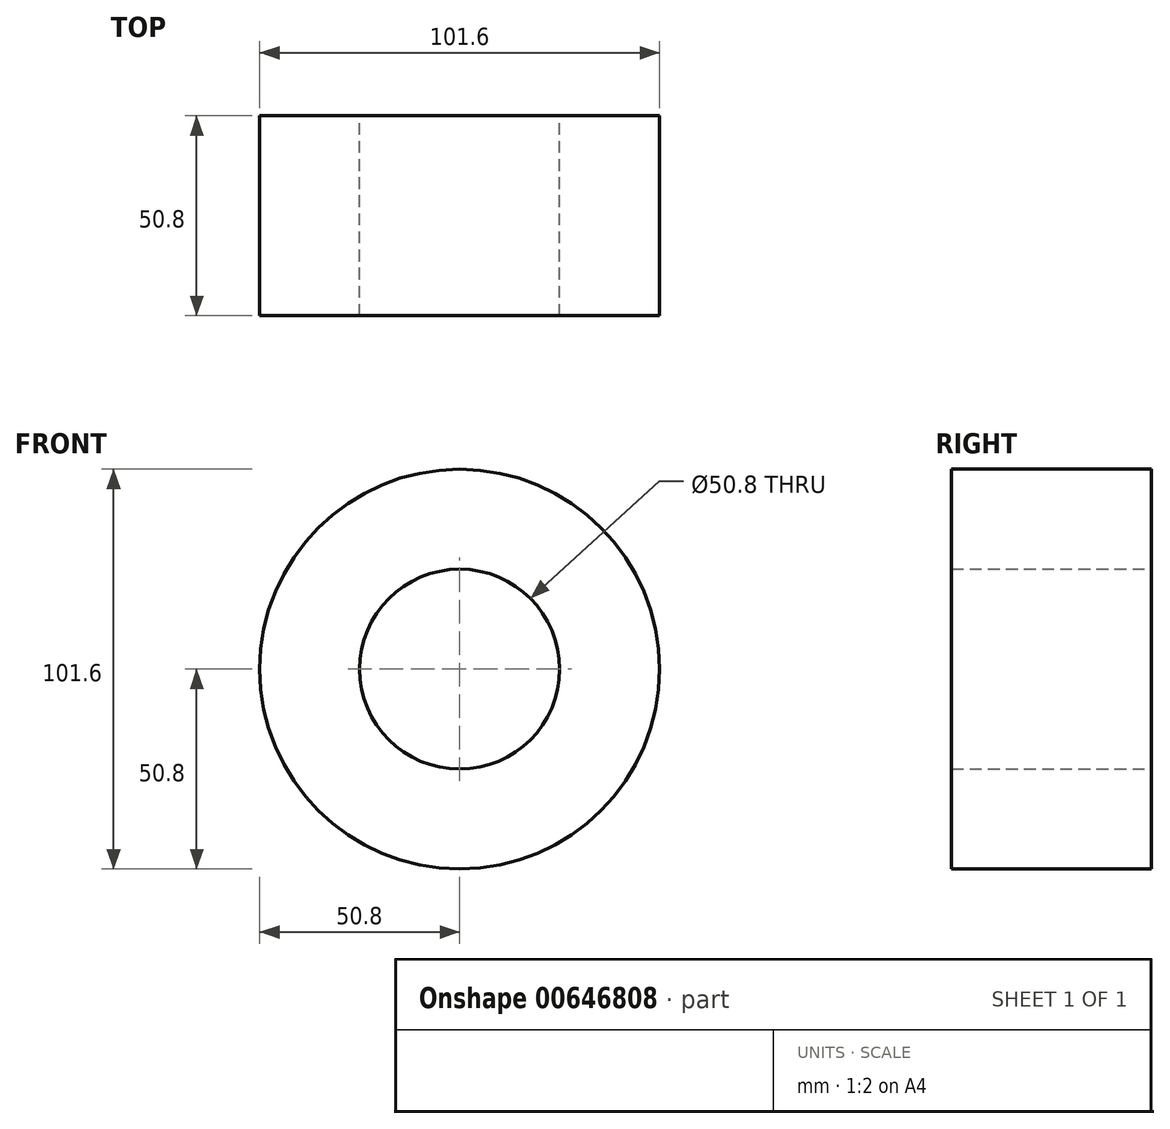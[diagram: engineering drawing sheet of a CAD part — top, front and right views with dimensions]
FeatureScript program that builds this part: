
annotation { "Feature Type Name" : "Feature", "Feature Type Description" : "" }
export const myFeature = defineFeature(function(context is Context, id is Id, definition is map)
    precondition{}
    {
        {
            var Q0;
            Q0=qCreatedBy(makeId("Front.planeOp"),FACE);
            var sketch = newSketch(context, id + "F0", { "sketchPlane" : qUnion([Q0])});
            skCircle(sketch, "E0", {"center": v(0, 0) * mm, "radius": 25.4 * mm});
            skCircle(sketch, "E1", {"center": v(0, 0) * mm, "radius": 50.8 * mm});
            skSolve(sketch);
        }
        {
            var Q0;
            Q0=makeQuery(id+"F0.imprint","IMPRINT",FACE,{"disambiguationData":[TD([[makeQuery(id+"F0.imprint","IMPRINT",EDGE,{"derivedFrom":sQuery(id+"F0.wireOp",EDGE,"E0")}),-1.0]])]});
            extrude(context, id + "F1", {"entities" : qUnion([Q0]), "depth" : 50.8 * mm, "offsetDistance" : 25.4 * mm});
        }
    });
